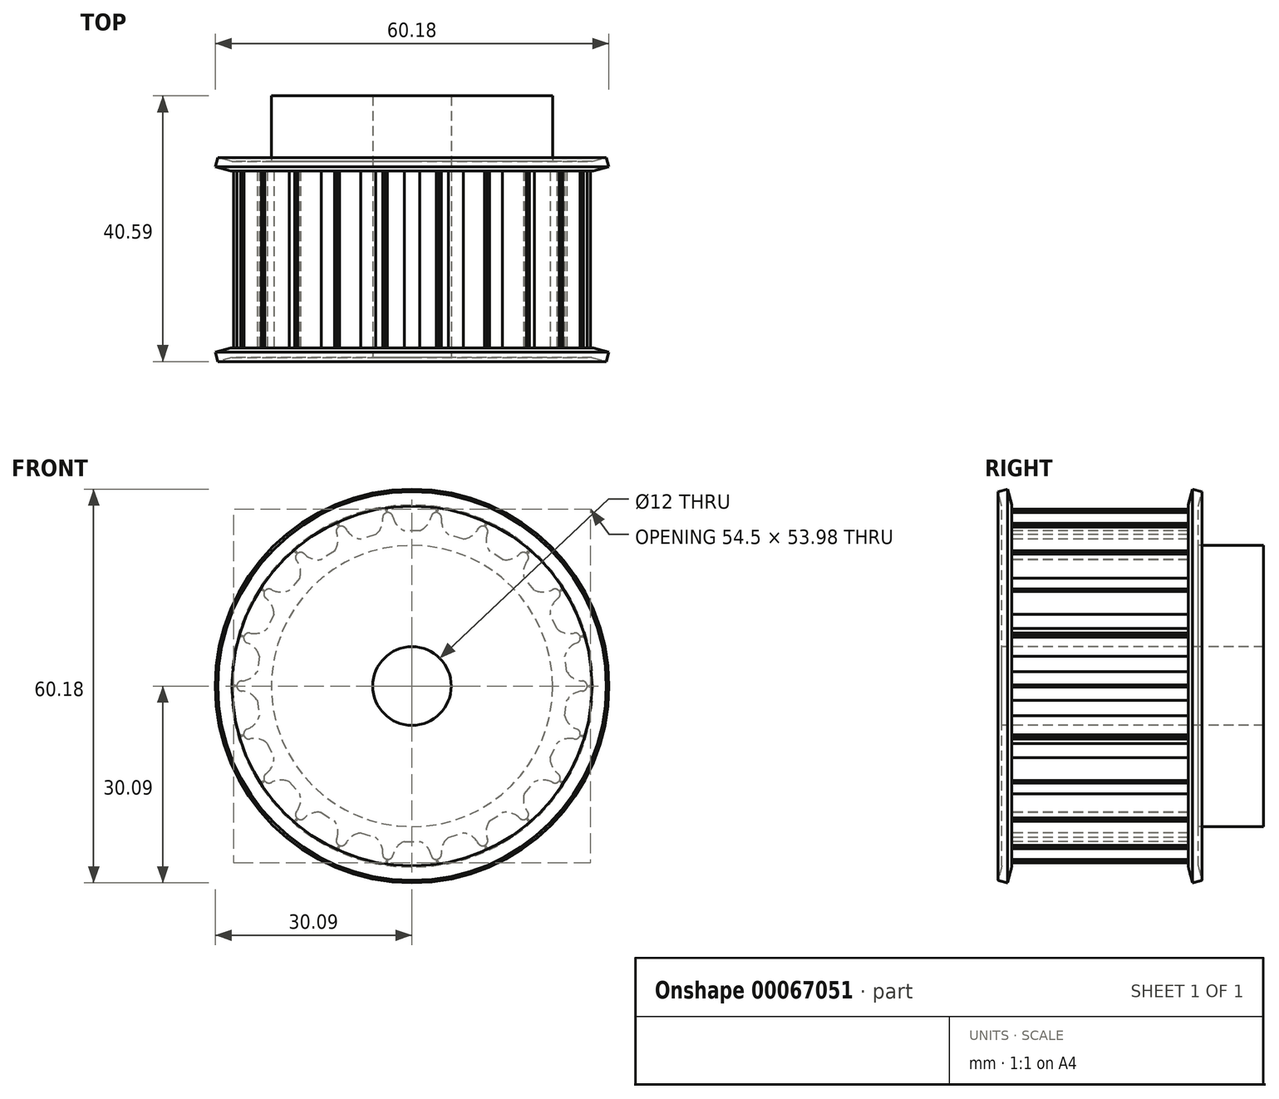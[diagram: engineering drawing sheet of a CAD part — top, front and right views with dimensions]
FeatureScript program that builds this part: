
annotation { "Feature Type Name" : "Feature", "Feature Type Description" : "" }
export const myFeature = defineFeature(function(context is Context, id is Id, definition is map)
    precondition{}
    {
        {
            var Q0;
            Q0=qCreatedBy(makeId("Right.planeOp"),FACE);
            var sketch = newSketch(context, id + "F0", { "sketchPlane" : qUnion([Q0])});
            skLineSegment(sketch, "E0", {"start": v(-21.52, 0) * mm, "end": v(23.89, 0) * mm, "construction": true});
            skLineSegment(sketch, "E1", {"start": v(0, 6) * mm, "end": v(0, 27.25) * mm});
            skLineSegment(sketch, "E2", {"start": v(0, 27.25) * mm, "end": v(30, 27.25) * mm});
            skLineSegment(sketch, "E3", {"start": v(30, 27.25) * mm, "end": v(30, 21.5) * mm});
            skLineSegment(sketch, "E4", {"start": v(30, 21.5) * mm, "end": v(40, 21.5) * mm});
            skLineSegment(sketch, "E5", {"start": v(40, 21.5) * mm, "end": v(40, 6) * mm});
            skLineSegment(sketch, "E6", {"start": v(40, 6) * mm, "end": v(0, 6) * mm});
            skSolve(sketch);
        }
        {
            var Q0;
            Q0=qSketchRegion(id+"F0",true);
            var Q1;
            Q1=sQuery(id+"F0.wireOp",EDGE,"E0");
            revolve(context, id + "F1", {"entities" : qUnion([Q0]), "axis" : qUnion([Q1]), "revolveType" : RevolveType.FULL});
        }
        {
            var Q0;
            Q0=makeQuery(id+"F1.opRevolve","SWEPT_FACE",FACE,{"disambiguationData":[OSD([sQuery(id+"F0.wireOp",EDGE,"E1")])]});
            var sketch = newSketch(context, id + "F2", { "sketchPlane" : qUnion([Q0])});
            skArc(sketch, "E7", {"start": v(-2.94, 25.9) * mm, "mid": v(-2.33, 24.61) * mm, "end": v(-1.2, 23.75) * mm});
            skLineSegment(sketch, "E8.bottom", {"start": v(-3.75, 28.5) * mm, "end": v(3.75, 28.5) * mm});
            skLineSegment(sketch, "E8.top", {"start": v(-3.75, 26.5) * mm, "end": v(-3.67, 26.5) * mm});
            skLineSegment(sketch, "E8.left", {"start": v(-3.75, 28.5) * mm, "end": v(-3.75, 26.5) * mm});
            skLineSegment(sketch, "E8.right", {"start": v(3.75, 28.5) * mm, "end": v(3.75, 26.5) * mm});
            skArc(sketch, "E9.filletArc", {"start": v(-2.94, 25.9) * mm, "mid": v(-3.2, 26.33) * mm, "end": v(-3.67, 26.5) * mm});
            skLineSegment(sketch, "E10", {"start": v(3.67, 26.5) * mm, "end": v(3.75, 26.5) * mm});
            skPoint(sketch, "E11.visualSharp", {"position": v(3, 26.5) * mm});
            skArc(sketch, "E11.filletArc", {"start": v(3.67, 26.5) * mm, "mid": v(3.2, 26.33) * mm, "end": v(2.94, 25.9) * mm});
            skLineSegment(sketch, "E12", {"start": v(-1.2, 23.75) * mm, "end": v(1.2, 23.75) * mm});
            skArc(sketch, "E13.trimOffspring", {"start": v(1.2, 23.75) * mm, "mid": v(2.33, 24.61) * mm, "end": v(2.94, 25.9) * mm});
            skLineSegment(sketch, "E14.1.0", {"start": v(-11.63, 26.29) * mm, "end": v(-4.43, 28.4) * mm});
            skLineSegment(sketch, "E14.1.1", {"start": v(-11.63, 26.29) * mm, "end": v(-11.06, 24.37) * mm});
            skArc(sketch, "E14.1.2", {"start": v(-10.12, 24.02) * mm, "mid": v(-10.49, 24.36) * mm, "end": v(-11, 24.4) * mm});
            skArc(sketch, "E14.1.3", {"start": v(-10.12, 24.02) * mm, "mid": v(-9.17, 22.96) * mm, "end": v(-7.84, 22.45) * mm});
            skLineSegment(sketch, "E14.1.4", {"start": v(-7.84, 22.45) * mm, "end": v(-5.54, 23.13) * mm});
            skArc(sketch, "E14.1.5", {"start": v(-5.54, 23.13) * mm, "mid": v(-4.7, 24.27) * mm, "end": v(-4.48, 25.68) * mm});
            skPoint(sketch, "E14.1.6", {"position": v(-4.59, 26.27) * mm});
            skLineSegment(sketch, "E14.1.7", {"start": v(-4.43, 28.4) * mm, "end": v(-3.87, 26.48) * mm});
            skArc(sketch, "E14.1.8", {"start": v(-3.94, 26.46) * mm, "mid": v(-4.35, 26.17) * mm, "end": v(-4.48, 25.68) * mm});
            skLineSegment(sketch, "E14.2.0", {"start": v(-18.56, 21.95) * mm, "end": v(-12.25, 26) * mm});
            skLineSegment(sketch, "E14.2.1", {"start": v(-18.56, 21.95) * mm, "end": v(-17.48, 20.27) * mm});
            skArc(sketch, "E14.2.2", {"start": v(-16.48, 20.2) * mm, "mid": v(-16.93, 20.42) * mm, "end": v(-17.42, 20.3) * mm});
            skArc(sketch, "E14.2.3", {"start": v(-16.48, 20.2) * mm, "mid": v(-15.27, 19.44) * mm, "end": v(-13.85, 19.33) * mm});
            skLineSegment(sketch, "E14.2.4", {"start": v(-13.85, 19.33) * mm, "end": v(-11.83, 20.63) * mm});
            skArc(sketch, "E14.2.5", {"start": v(-11.83, 20.63) * mm, "mid": v(-11.34, 21.97) * mm, "end": v(-11.53, 23.38) * mm});
            skPoint(sketch, "E14.2.6", {"position": v(-11.8, 23.92) * mm});
            skLineSegment(sketch, "E14.2.7", {"start": v(-12.25, 26) * mm, "end": v(-11.17, 24.32) * mm});
            skArc(sketch, "E14.2.8", {"start": v(-11.24, 24.28) * mm, "mid": v(-11.54, 23.88) * mm, "end": v(-11.53, 23.38) * mm});
            skLineSegment(sketch, "E14.3.0", {"start": v(-24, 15.83) * mm, "end": v(-19.08, 21.5) * mm});
            skLineSegment(sketch, "E14.3.1", {"start": v(-24, 15.83) * mm, "end": v(-22.48, 14.52) * mm});
            skArc(sketch, "E14.3.2", {"start": v(-21.5, 14.74) * mm, "mid": v(-22, 14.82) * mm, "end": v(-22.43, 14.58) * mm});
            skArc(sketch, "E14.3.3", {"start": v(-21.5, 14.74) * mm, "mid": v(-20.13, 14.36) * mm, "end": v(-18.73, 14.65) * mm});
            skLineSegment(sketch, "E14.3.4", {"start": v(-18.73, 14.65) * mm, "end": v(-17.16, 16.46) * mm});
            skArc(sketch, "E14.3.5", {"start": v(-17.16, 16.46) * mm, "mid": v(-17.07, 17.88) * mm, "end": v(-17.65, 19.18) * mm});
            skPoint(sketch, "E14.3.6", {"position": v(-18.06, 19.62) * mm});
            skLineSegment(sketch, "E14.3.7", {"start": v(-19.08, 21.5) * mm, "end": v(-17.57, 20.19) * mm});
            skArc(sketch, "E14.3.8", {"start": v(-17.62, 20.13) * mm, "mid": v(-17.8, 19.66) * mm, "end": v(-17.65, 19.18) * mm});
            skLineSegment(sketch, "E14.4.0", {"start": v(-27.48, 8.43) * mm, "end": v(-24.37, 15.25) * mm});
            skLineSegment(sketch, "E14.4.1", {"start": v(-27.48, 8.43) * mm, "end": v(-25.66, 7.6) * mm});
            skArc(sketch, "E14.4.2", {"start": v(-24.78, 8.09) * mm, "mid": v(-25.28, 8.03) * mm, "end": v(-25.63, 7.67) * mm});
            skArc(sketch, "E14.4.3", {"start": v(-24.78, 8.09) * mm, "mid": v(-23.36, 8.1) * mm, "end": v(-22.1, 8.78) * mm});
            skLineSegment(sketch, "E14.4.4", {"start": v(-22.1, 8.78) * mm, "end": v(-21.1, 10.96) * mm});
            skArc(sketch, "E14.4.5", {"start": v(-21.1, 10.96) * mm, "mid": v(-21.42, 12.35) * mm, "end": v(-22.34, 13.43) * mm});
            skPoint(sketch, "E14.4.6", {"position": v(-22.86, 13.74) * mm});
            skLineSegment(sketch, "E14.4.7", {"start": v(-24.37, 15.25) * mm, "end": v(-22.55, 14.42) * mm});
            skArc(sketch, "E14.4.8", {"start": v(-22.58, 14.35) * mm, "mid": v(-22.62, 13.85) * mm, "end": v(-22.34, 13.43) * mm});
            skLineSegment(sketch, "E14.5.0", {"start": v(-28.74, 0.34) * mm, "end": v(-27.68, 7.77) * mm});
            skLineSegment(sketch, "E14.5.1", {"start": v(-28.74, 0.34) * mm, "end": v(-26.76, 0.06) * mm});
            skArc(sketch, "E14.5.2", {"start": v(-26.05, 0.78) * mm, "mid": v(-26.52, 0.58) * mm, "end": v(-26.75, 0.13) * mm});
            skArc(sketch, "E14.5.3", {"start": v(-26.05, 0.78) * mm, "mid": v(-24.7, 1.2) * mm, "end": v(-23.68, 2.2) * mm});
            skLineSegment(sketch, "E14.5.4", {"start": v(-23.68, 2.2) * mm, "end": v(-23.34, 4.57) * mm});
            skArc(sketch, "E14.5.5", {"start": v(-23.34, 4.57) * mm, "mid": v(-24.03, 5.81) * mm, "end": v(-25.22, 6.6) * mm});
            skPoint(sketch, "E14.5.6", {"position": v(-25.8, 6.74) * mm});
            skLineSegment(sketch, "E14.5.7", {"start": v(-27.68, 7.77) * mm, "end": v(-25.7, 7.48) * mm});
            skArc(sketch, "E14.5.8", {"start": v(-25.7, 7.4) * mm, "mid": v(-25.6, 6.91) * mm, "end": v(-25.22, 6.6) * mm});
            skLineSegment(sketch, "E14.6.0", {"start": v(-27.68, -7.77) * mm, "end": v(-28.74, -0.34) * mm});
            skLineSegment(sketch, "E14.6.1", {"start": v(-27.68, -7.77) * mm, "end": v(-25.7, -7.48) * mm});
            skArc(sketch, "E14.6.2", {"start": v(-25.22, -6.6) * mm, "mid": v(-25.6, -6.91) * mm, "end": v(-25.7, -7.4) * mm});
            skArc(sketch, "E14.6.3", {"start": v(-25.22, -6.6) * mm, "mid": v(-24.03, -5.81) * mm, "end": v(-23.34, -4.57) * mm});
            skLineSegment(sketch, "E14.6.4", {"start": v(-23.34, -4.57) * mm, "end": v(-23.68, -2.2) * mm});
            skArc(sketch, "E14.6.5", {"start": v(-23.68, -2.2) * mm, "mid": v(-24.7, -1.2) * mm, "end": v(-26.05, -0.78) * mm});
            skPoint(sketch, "E14.6.6", {"position": v(-26.66, -0.8) * mm});
            skLineSegment(sketch, "E14.6.7", {"start": v(-28.74, -0.34) * mm, "end": v(-26.76, -0.06) * mm});
            skArc(sketch, "E14.6.8", {"start": v(-26.75, -0.13) * mm, "mid": v(-26.52, -0.58) * mm, "end": v(-26.05, -0.78) * mm});
            skLineSegment(sketch, "E14.7.0", {"start": v(-24.37, -15.25) * mm, "end": v(-27.48, -8.43) * mm});
            skLineSegment(sketch, "E14.7.1", {"start": v(-24.37, -15.25) * mm, "end": v(-22.55, -14.42) * mm});
            skArc(sketch, "E14.7.2", {"start": v(-22.34, -13.43) * mm, "mid": v(-22.62, -13.85) * mm, "end": v(-22.58, -14.35) * mm});
            skArc(sketch, "E14.7.3", {"start": v(-22.34, -13.43) * mm, "mid": v(-21.42, -12.35) * mm, "end": v(-21.1, -10.96) * mm});
            skLineSegment(sketch, "E14.7.4", {"start": v(-21.1, -10.96) * mm, "end": v(-22.1, -8.78) * mm});
            skArc(sketch, "E14.7.5", {"start": v(-22.1, -8.78) * mm, "mid": v(-23.36, -8.1) * mm, "end": v(-24.78, -8.09) * mm});
            skPoint(sketch, "E14.7.6", {"position": v(-25.35, -8.28) * mm});
            skLineSegment(sketch, "E14.7.7", {"start": v(-27.48, -8.43) * mm, "end": v(-25.66, -7.6) * mm});
            skArc(sketch, "E14.7.8", {"start": v(-25.63, -7.67) * mm, "mid": v(-25.28, -8.03) * mm, "end": v(-24.78, -8.09) * mm});
            skLineSegment(sketch, "E14.8.0", {"start": v(-19.08, -21.5) * mm, "end": v(-24, -15.83) * mm});
            skLineSegment(sketch, "E14.8.1", {"start": v(-19.08, -21.5) * mm, "end": v(-17.57, -20.19) * mm});
            skArc(sketch, "E14.8.2", {"start": v(-17.65, -19.18) * mm, "mid": v(-17.8, -19.66) * mm, "end": v(-17.62, -20.13) * mm});
            skArc(sketch, "E14.8.3", {"start": v(-17.65, -19.18) * mm, "mid": v(-17.07, -17.88) * mm, "end": v(-17.16, -16.46) * mm});
            skLineSegment(sketch, "E14.8.4", {"start": v(-17.16, -16.46) * mm, "end": v(-18.73, -14.65) * mm});
            skArc(sketch, "E14.8.5", {"start": v(-18.73, -14.65) * mm, "mid": v(-20.13, -14.36) * mm, "end": v(-21.5, -14.74) * mm});
            skPoint(sketch, "E14.8.6", {"position": v(-22, -15.09) * mm});
            skLineSegment(sketch, "E14.8.7", {"start": v(-24, -15.83) * mm, "end": v(-22.48, -14.52) * mm});
            skArc(sketch, "E14.8.8", {"start": v(-22.43, -14.58) * mm, "mid": v(-22, -14.82) * mm, "end": v(-21.5, -14.74) * mm});
            skLineSegment(sketch, "E14.9.0", {"start": v(-12.25, -26) * mm, "end": v(-18.56, -21.95) * mm});
            skLineSegment(sketch, "E14.9.1", {"start": v(-12.25, -26) * mm, "end": v(-11.17, -24.32) * mm});
            skArc(sketch, "E14.9.2", {"start": v(-11.53, -23.38) * mm, "mid": v(-11.54, -23.88) * mm, "end": v(-11.24, -24.28) * mm});
            skArc(sketch, "E14.9.3", {"start": v(-11.53, -23.38) * mm, "mid": v(-11.34, -21.97) * mm, "end": v(-11.83, -20.63) * mm});
            skLineSegment(sketch, "E14.9.4", {"start": v(-11.83, -20.63) * mm, "end": v(-13.85, -19.33) * mm});
            skArc(sketch, "E14.9.5", {"start": v(-13.85, -19.33) * mm, "mid": v(-15.27, -19.44) * mm, "end": v(-16.48, -20.2) * mm});
            skPoint(sketch, "E14.9.6", {"position": v(-16.85, -20.67) * mm});
            skLineSegment(sketch, "E14.9.7", {"start": v(-18.56, -21.95) * mm, "end": v(-17.48, -20.27) * mm});
            skArc(sketch, "E14.9.8", {"start": v(-17.42, -20.3) * mm, "mid": v(-16.93, -20.42) * mm, "end": v(-16.48, -20.2) * mm});
            skLineSegment(sketch, "E14.10.0", {"start": v(-4.43, -28.4) * mm, "end": v(-11.63, -26.29) * mm});
            skLineSegment(sketch, "E14.10.1", {"start": v(-4.43, -28.4) * mm, "end": v(-3.87, -26.48) * mm});
            skArc(sketch, "E14.10.2", {"start": v(-4.48, -25.68) * mm, "mid": v(-4.35, -26.17) * mm, "end": v(-3.94, -26.46) * mm});
            skArc(sketch, "E14.10.3", {"start": v(-4.48, -25.68) * mm, "mid": v(-4.7, -24.27) * mm, "end": v(-5.54, -23.13) * mm});
            skLineSegment(sketch, "E14.10.4", {"start": v(-5.54, -23.13) * mm, "end": v(-7.84, -22.45) * mm});
            skArc(sketch, "E14.10.5", {"start": v(-7.84, -22.45) * mm, "mid": v(-9.17, -22.96) * mm, "end": v(-10.12, -24.02) * mm});
            skPoint(sketch, "E14.10.6", {"position": v(-10.34, -24.58) * mm});
            skLineSegment(sketch, "E14.10.7", {"start": v(-11.63, -26.29) * mm, "end": v(-11.06, -24.37) * mm});
            skArc(sketch, "E14.10.8", {"start": v(-11, -24.4) * mm, "mid": v(-10.49, -24.36) * mm, "end": v(-10.12, -24.02) * mm});
            skLineSegment(sketch, "E14.11.0", {"start": v(3.75, -28.5) * mm, "end": v(-3.75, -28.5) * mm});
            skLineSegment(sketch, "E14.11.1", {"start": v(3.75, -28.5) * mm, "end": v(3.75, -26.5) * mm});
            skArc(sketch, "E14.11.2", {"start": v(2.94, -25.9) * mm, "mid": v(3.2, -26.33) * mm, "end": v(3.67, -26.5) * mm});
            skArc(sketch, "E14.11.3", {"start": v(2.94, -25.9) * mm, "mid": v(2.33, -24.61) * mm, "end": v(1.2, -23.75) * mm});
            skLineSegment(sketch, "E14.11.4", {"start": v(1.2, -23.75) * mm, "end": v(-1.2, -23.75) * mm});
            skArc(sketch, "E14.11.5", {"start": v(-1.2, -23.75) * mm, "mid": v(-2.33, -24.61) * mm, "end": v(-2.94, -25.9) * mm});
            skPoint(sketch, "E14.11.6", {"position": v(-3, -26.5) * mm});
            skLineSegment(sketch, "E14.11.7", {"start": v(-3.75, -28.5) * mm, "end": v(-3.75, -26.5) * mm});
            skArc(sketch, "E14.11.8", {"start": v(-3.67, -26.5) * mm, "mid": v(-3.2, -26.33) * mm, "end": v(-2.94, -25.9) * mm});
            skLineSegment(sketch, "E14.12.0", {"start": v(11.63, -26.29) * mm, "end": v(4.43, -28.4) * mm});
            skLineSegment(sketch, "E14.12.1", {"start": v(11.63, -26.29) * mm, "end": v(11.06, -24.37) * mm});
            skArc(sketch, "E14.12.2", {"start": v(10.12, -24.02) * mm, "mid": v(10.49, -24.36) * mm, "end": v(11, -24.4) * mm});
            skArc(sketch, "E14.12.3", {"start": v(10.12, -24.02) * mm, "mid": v(9.17, -22.96) * mm, "end": v(7.84, -22.45) * mm});
            skLineSegment(sketch, "E14.12.4", {"start": v(7.84, -22.45) * mm, "end": v(5.54, -23.13) * mm});
            skArc(sketch, "E14.12.5", {"start": v(5.54, -23.13) * mm, "mid": v(4.7, -24.27) * mm, "end": v(4.48, -25.68) * mm});
            skPoint(sketch, "E14.12.6", {"position": v(4.59, -26.27) * mm});
            skLineSegment(sketch, "E14.12.7", {"start": v(4.43, -28.4) * mm, "end": v(3.87, -26.48) * mm});
            skArc(sketch, "E14.12.8", {"start": v(3.94, -26.46) * mm, "mid": v(4.35, -26.17) * mm, "end": v(4.48, -25.68) * mm});
            skLineSegment(sketch, "E14.13.0", {"start": v(18.56, -21.95) * mm, "end": v(12.25, -26) * mm});
            skLineSegment(sketch, "E14.13.1", {"start": v(18.56, -21.95) * mm, "end": v(17.48, -20.27) * mm});
            skArc(sketch, "E14.13.2", {"start": v(16.48, -20.2) * mm, "mid": v(16.93, -20.42) * mm, "end": v(17.42, -20.3) * mm});
            skArc(sketch, "E14.13.3", {"start": v(16.48, -20.2) * mm, "mid": v(15.27, -19.44) * mm, "end": v(13.85, -19.33) * mm});
            skLineSegment(sketch, "E14.13.4", {"start": v(13.85, -19.33) * mm, "end": v(11.83, -20.63) * mm});
            skArc(sketch, "E14.13.5", {"start": v(11.83, -20.63) * mm, "mid": v(11.34, -21.97) * mm, "end": v(11.53, -23.38) * mm});
            skPoint(sketch, "E14.13.6", {"position": v(11.8, -23.92) * mm});
            skLineSegment(sketch, "E14.13.7", {"start": v(12.25, -26) * mm, "end": v(11.17, -24.32) * mm});
            skArc(sketch, "E14.13.8", {"start": v(11.24, -24.28) * mm, "mid": v(11.54, -23.88) * mm, "end": v(11.53, -23.38) * mm});
            skLineSegment(sketch, "E14.14.0", {"start": v(24, -15.83) * mm, "end": v(19.08, -21.5) * mm});
            skLineSegment(sketch, "E14.14.1", {"start": v(24, -15.83) * mm, "end": v(22.48, -14.52) * mm});
            skArc(sketch, "E14.14.2", {"start": v(21.5, -14.74) * mm, "mid": v(22, -14.82) * mm, "end": v(22.43, -14.58) * mm});
            skArc(sketch, "E14.14.3", {"start": v(21.5, -14.74) * mm, "mid": v(20.13, -14.36) * mm, "end": v(18.73, -14.65) * mm});
            skLineSegment(sketch, "E14.14.4", {"start": v(18.73, -14.65) * mm, "end": v(17.16, -16.46) * mm});
            skArc(sketch, "E14.14.5", {"start": v(17.16, -16.46) * mm, "mid": v(17.07, -17.88) * mm, "end": v(17.65, -19.18) * mm});
            skPoint(sketch, "E14.14.6", {"position": v(18.06, -19.62) * mm});
            skLineSegment(sketch, "E14.14.7", {"start": v(19.08, -21.5) * mm, "end": v(17.57, -20.19) * mm});
            skArc(sketch, "E14.14.8", {"start": v(17.62, -20.13) * mm, "mid": v(17.8, -19.66) * mm, "end": v(17.65, -19.18) * mm});
            skLineSegment(sketch, "E14.15.0", {"start": v(27.48, -8.43) * mm, "end": v(24.37, -15.25) * mm});
            skLineSegment(sketch, "E14.15.1", {"start": v(27.48, -8.43) * mm, "end": v(25.66, -7.6) * mm});
            skArc(sketch, "E14.15.2", {"start": v(24.78, -8.09) * mm, "mid": v(25.28, -8.03) * mm, "end": v(25.63, -7.67) * mm});
            skArc(sketch, "E14.15.3", {"start": v(24.78, -8.09) * mm, "mid": v(23.36, -8.1) * mm, "end": v(22.1, -8.78) * mm});
            skLineSegment(sketch, "E14.15.4", {"start": v(22.1, -8.78) * mm, "end": v(21.1, -10.96) * mm});
            skArc(sketch, "E14.15.5", {"start": v(21.1, -10.96) * mm, "mid": v(21.42, -12.35) * mm, "end": v(22.34, -13.43) * mm});
            skPoint(sketch, "E14.15.6", {"position": v(22.86, -13.74) * mm});
            skLineSegment(sketch, "E14.15.7", {"start": v(24.37, -15.25) * mm, "end": v(22.55, -14.42) * mm});
            skArc(sketch, "E14.15.8", {"start": v(22.58, -14.35) * mm, "mid": v(22.62, -13.85) * mm, "end": v(22.34, -13.43) * mm});
            skLineSegment(sketch, "E14.16.0", {"start": v(28.74, -0.34) * mm, "end": v(27.68, -7.77) * mm});
            skLineSegment(sketch, "E14.16.1", {"start": v(28.74, -0.34) * mm, "end": v(26.76, -0.06) * mm});
            skArc(sketch, "E14.16.2", {"start": v(26.05, -0.78) * mm, "mid": v(26.52, -0.58) * mm, "end": v(26.75, -0.13) * mm});
            skArc(sketch, "E14.16.3", {"start": v(26.05, -0.78) * mm, "mid": v(24.7, -1.2) * mm, "end": v(23.68, -2.2) * mm});
            skLineSegment(sketch, "E14.16.4", {"start": v(23.68, -2.2) * mm, "end": v(23.34, -4.57) * mm});
            skArc(sketch, "E14.16.5", {"start": v(23.34, -4.57) * mm, "mid": v(24.03, -5.81) * mm, "end": v(25.22, -6.6) * mm});
            skPoint(sketch, "E14.16.6", {"position": v(25.8, -6.74) * mm});
            skLineSegment(sketch, "E14.16.7", {"start": v(27.68, -7.77) * mm, "end": v(25.7, -7.48) * mm});
            skArc(sketch, "E14.16.8", {"start": v(25.7, -7.4) * mm, "mid": v(25.6, -6.91) * mm, "end": v(25.22, -6.6) * mm});
            skLineSegment(sketch, "E14.17.0", {"start": v(27.68, 7.77) * mm, "end": v(28.74, 0.34) * mm});
            skLineSegment(sketch, "E14.17.1", {"start": v(27.68, 7.77) * mm, "end": v(25.7, 7.48) * mm});
            skArc(sketch, "E14.17.2", {"start": v(25.22, 6.6) * mm, "mid": v(25.6, 6.91) * mm, "end": v(25.7, 7.4) * mm});
            skArc(sketch, "E14.17.3", {"start": v(25.22, 6.6) * mm, "mid": v(24.03, 5.81) * mm, "end": v(23.34, 4.57) * mm});
            skLineSegment(sketch, "E14.17.4", {"start": v(23.34, 4.57) * mm, "end": v(23.68, 2.2) * mm});
            skArc(sketch, "E14.17.5", {"start": v(23.68, 2.2) * mm, "mid": v(24.7, 1.2) * mm, "end": v(26.05, 0.78) * mm});
            skPoint(sketch, "E14.17.6", {"position": v(26.66, 0.8) * mm});
            skLineSegment(sketch, "E14.17.7", {"start": v(28.74, 0.34) * mm, "end": v(26.76, 0.06) * mm});
            skArc(sketch, "E14.17.8", {"start": v(26.75, 0.13) * mm, "mid": v(26.52, 0.58) * mm, "end": v(26.05, 0.78) * mm});
            skLineSegment(sketch, "E14.18.0", {"start": v(24.37, 15.25) * mm, "end": v(27.48, 8.43) * mm});
            skLineSegment(sketch, "E14.18.1", {"start": v(24.37, 15.25) * mm, "end": v(22.55, 14.42) * mm});
            skArc(sketch, "E14.18.2", {"start": v(22.34, 13.43) * mm, "mid": v(22.62, 13.85) * mm, "end": v(22.58, 14.35) * mm});
            skArc(sketch, "E14.18.3", {"start": v(22.34, 13.43) * mm, "mid": v(21.42, 12.35) * mm, "end": v(21.1, 10.96) * mm});
            skLineSegment(sketch, "E14.18.4", {"start": v(21.1, 10.96) * mm, "end": v(22.1, 8.78) * mm});
            skArc(sketch, "E14.18.5", {"start": v(22.1, 8.78) * mm, "mid": v(23.36, 8.1) * mm, "end": v(24.78, 8.09) * mm});
            skPoint(sketch, "E14.18.6", {"position": v(25.35, 8.28) * mm});
            skLineSegment(sketch, "E14.18.7", {"start": v(27.48, 8.43) * mm, "end": v(25.66, 7.6) * mm});
            skArc(sketch, "E14.18.8", {"start": v(25.63, 7.67) * mm, "mid": v(25.28, 8.03) * mm, "end": v(24.78, 8.09) * mm});
            skLineSegment(sketch, "E14.19.0", {"start": v(19.08, 21.5) * mm, "end": v(24, 15.83) * mm});
            skLineSegment(sketch, "E14.19.1", {"start": v(19.08, 21.5) * mm, "end": v(17.57, 20.19) * mm});
            skArc(sketch, "E14.19.2", {"start": v(17.65, 19.18) * mm, "mid": v(17.8, 19.66) * mm, "end": v(17.62, 20.13) * mm});
            skArc(sketch, "E14.19.3", {"start": v(17.65, 19.18) * mm, "mid": v(17.07, 17.88) * mm, "end": v(17.16, 16.46) * mm});
            skLineSegment(sketch, "E14.19.4", {"start": v(17.16, 16.46) * mm, "end": v(18.73, 14.65) * mm});
            skArc(sketch, "E14.19.5", {"start": v(18.73, 14.65) * mm, "mid": v(20.13, 14.36) * mm, "end": v(21.5, 14.74) * mm});
            skPoint(sketch, "E14.19.6", {"position": v(22, 15.09) * mm});
            skLineSegment(sketch, "E14.19.7", {"start": v(24, 15.83) * mm, "end": v(22.48, 14.52) * mm});
            skArc(sketch, "E14.19.8", {"start": v(22.43, 14.58) * mm, "mid": v(22, 14.82) * mm, "end": v(21.5, 14.74) * mm});
            skLineSegment(sketch, "E14.20.0", {"start": v(12.25, 26) * mm, "end": v(18.56, 21.95) * mm});
            skLineSegment(sketch, "E14.20.1", {"start": v(12.25, 26) * mm, "end": v(11.17, 24.32) * mm});
            skArc(sketch, "E14.20.2", {"start": v(11.53, 23.38) * mm, "mid": v(11.54, 23.88) * mm, "end": v(11.24, 24.28) * mm});
            skArc(sketch, "E14.20.3", {"start": v(11.53, 23.38) * mm, "mid": v(11.34, 21.97) * mm, "end": v(11.83, 20.63) * mm});
            skLineSegment(sketch, "E14.20.4", {"start": v(11.83, 20.63) * mm, "end": v(13.85, 19.33) * mm});
            skArc(sketch, "E14.20.5", {"start": v(13.85, 19.33) * mm, "mid": v(15.27, 19.44) * mm, "end": v(16.48, 20.2) * mm});
            skPoint(sketch, "E14.20.6", {"position": v(16.85, 20.67) * mm});
            skLineSegment(sketch, "E14.20.7", {"start": v(18.56, 21.95) * mm, "end": v(17.48, 20.27) * mm});
            skArc(sketch, "E14.20.8", {"start": v(17.42, 20.3) * mm, "mid": v(16.93, 20.42) * mm, "end": v(16.48, 20.2) * mm});
            skLineSegment(sketch, "E14.21.0", {"start": v(4.43, 28.4) * mm, "end": v(11.63, 26.29) * mm});
            skLineSegment(sketch, "E14.21.1", {"start": v(4.43, 28.4) * mm, "end": v(3.87, 26.48) * mm});
            skArc(sketch, "E14.21.2", {"start": v(4.48, 25.68) * mm, "mid": v(4.35, 26.17) * mm, "end": v(3.94, 26.46) * mm});
            skArc(sketch, "E14.21.3", {"start": v(4.48, 25.68) * mm, "mid": v(4.7, 24.27) * mm, "end": v(5.54, 23.13) * mm});
            skLineSegment(sketch, "E14.21.4", {"start": v(5.54, 23.13) * mm, "end": v(7.84, 22.45) * mm});
            skArc(sketch, "E14.21.5", {"start": v(7.84, 22.45) * mm, "mid": v(9.17, 22.96) * mm, "end": v(10.12, 24.02) * mm});
            skPoint(sketch, "E14.21.6", {"position": v(10.34, 24.58) * mm});
            skLineSegment(sketch, "E14.21.7", {"start": v(11.63, 26.29) * mm, "end": v(11.06, 24.37) * mm});
            skArc(sketch, "E14.21.8", {"start": v(11, 24.4) * mm, "mid": v(10.49, 24.36) * mm, "end": v(10.12, 24.02) * mm});
            skPoint(sketch, "E14.center", {"position": v(0, 0) * mm});
            skLineSegment(sketch, "E15", {"start": v(-11.06, 24.37) * mm, "end": v(-11, 24.4) * mm});
            skLineSegment(sketch, "E16", {"start": v(-11.24, 24.28) * mm, "end": v(-11.17, 24.32) * mm});
            skLineSegment(sketch, "E17", {"start": v(-17.48, 20.27) * mm, "end": v(-17.42, 20.3) * mm});
            skLineSegment(sketch, "E18", {"start": v(-17.62, 20.13) * mm, "end": v(-17.57, 20.19) * mm});
            skLineSegment(sketch, "E19", {"start": v(-3.94, 26.46) * mm, "end": v(-3.87, 26.48) * mm});
            skLineSegment(sketch, "E20", {"start": v(3.87, 26.48) * mm, "end": v(3.94, 26.46) * mm});
            skLineSegment(sketch, "E21", {"start": v(11, 24.4) * mm, "end": v(11.06, 24.37) * mm});
            skLineSegment(sketch, "E22", {"start": v(11.17, 24.32) * mm, "end": v(11.24, 24.28) * mm});
            skLineSegment(sketch, "E23", {"start": v(17.42, 20.3) * mm, "end": v(17.48, 20.27) * mm});
            skLineSegment(sketch, "E24", {"start": v(17.57, 20.19) * mm, "end": v(17.62, 20.13) * mm});
            skLineSegment(sketch, "E25", {"start": v(22.43, 14.58) * mm, "end": v(22.48, 14.52) * mm});
            skLineSegment(sketch, "E26", {"start": v(22.55, 14.42) * mm, "end": v(22.58, 14.35) * mm});
            skLineSegment(sketch, "E27", {"start": v(25.63, 7.67) * mm, "end": v(25.66, 7.6) * mm});
            skLineSegment(sketch, "E28", {"start": v(25.7, 7.48) * mm, "end": v(25.7, 7.4) * mm});
            skLineSegment(sketch, "E29", {"start": v(26.75, 0.13) * mm, "end": v(26.76, 0.06) * mm});
            skLineSegment(sketch, "E30", {"start": v(26.76, -0.06) * mm, "end": v(26.75, -0.13) * mm});
            skLineSegment(sketch, "E31", {"start": v(25.7, -7.4) * mm, "end": v(25.7, -7.48) * mm});
            skLineSegment(sketch, "E32", {"start": v(25.66, -7.6) * mm, "end": v(25.63, -7.67) * mm});
            skLineSegment(sketch, "E33", {"start": v(22.58, -14.35) * mm, "end": v(22.55, -14.42) * mm});
            skLineSegment(sketch, "E34", {"start": v(22.48, -14.52) * mm, "end": v(22.43, -14.58) * mm});
            skLineSegment(sketch, "E35", {"start": v(17.42, -20.3) * mm, "end": v(17.48, -20.27) * mm});
            skLineSegment(sketch, "E36", {"start": v(17.57, -20.19) * mm, "end": v(17.62, -20.13) * mm});
            skLineSegment(sketch, "E37", {"start": v(11, -24.4) * mm, "end": v(11.06, -24.37) * mm});
            skLineSegment(sketch, "E38", {"start": v(11.17, -24.32) * mm, "end": v(11.24, -24.28) * mm});
            skLineSegment(sketch, "E39", {"start": v(3.67, -26.5) * mm, "end": v(3.75, -26.5) * mm});
            skLineSegment(sketch, "E40", {"start": v(3.87, -26.48) * mm, "end": v(3.94, -26.46) * mm});
            skLineSegment(sketch, "E41", {"start": v(-3.94, -26.46) * mm, "end": v(-3.87, -26.48) * mm});
            skLineSegment(sketch, "E42", {"start": v(-3.75, -26.5) * mm, "end": v(-3.67, -26.5) * mm});
            skLineSegment(sketch, "E43", {"start": v(-11.24, -24.28) * mm, "end": v(-11.17, -24.32) * mm});
            skLineSegment(sketch, "E44", {"start": v(-11.06, -24.37) * mm, "end": v(-11, -24.4) * mm});
            skLineSegment(sketch, "E45", {"start": v(-17.62, -20.13) * mm, "end": v(-17.57, -20.19) * mm});
            skLineSegment(sketch, "E46", {"start": v(-17.48, -20.27) * mm, "end": v(-17.42, -20.3) * mm});
            skLineSegment(sketch, "E47", {"start": v(-22.58, -14.35) * mm, "end": v(-22.55, -14.42) * mm});
            skLineSegment(sketch, "E48", {"start": v(-22.48, -14.52) * mm, "end": v(-22.43, -14.58) * mm});
            skLineSegment(sketch, "E49", {"start": v(-25.7, -7.4) * mm, "end": v(-25.7, -7.48) * mm});
            skLineSegment(sketch, "E50", {"start": v(-25.66, -7.6) * mm, "end": v(-25.63, -7.67) * mm});
            skLineSegment(sketch, "E51", {"start": v(-26.76, -0.06) * mm, "end": v(-26.75, -0.13) * mm});
            skLineSegment(sketch, "E52", {"start": v(-26.75, 0.13) * mm, "end": v(-26.76, 0.06) * mm});
            skLineSegment(sketch, "E53", {"start": v(-25.63, 7.67) * mm, "end": v(-25.66, 7.6) * mm});
            skLineSegment(sketch, "E54", {"start": v(-25.7, 7.48) * mm, "end": v(-25.7, 7.4) * mm});
            skLineSegment(sketch, "E55", {"start": v(-22.43, 14.58) * mm, "end": v(-22.48, 14.52) * mm});
            skLineSegment(sketch, "E56", {"start": v(-22.55, 14.42) * mm, "end": v(-22.58, 14.35) * mm});
            skSolve(sketch);
        }
        {
            var Q0;
            Q0=qSketchRegion(id+"F2",true);
            extrude(context, id + "F3", {"entities" : qUnion([Q0]), "operationType" : NewBodyOperationType.REMOVE, "endBound" : BoundingType.THROUGH_ALL, "oppositeDirection" : true, "depth" : 25.4 * mm});
        }
        {
            var Q0;
            Q0=qCreatedBy(makeId("Right.planeOp"),FACE);
            var sketch = newSketch(context, id + "F4", { "sketchPlane" : qUnion([Q0])});
            skLineSegment(sketch, "E57.bottom", {"start": v(0, 22.7) * mm, "end": v(1.5, 22.7) * mm});
            skLineSegment(sketch, "E57.top", {"start": v(0, 27.7) * mm, "end": v(1.5, 27.7) * mm});
            skLineSegment(sketch, "E57.left", {"start": v(0, 22.7) * mm, "end": v(0, 27.7) * mm});
            skLineSegment(sketch, "E57.right", {"start": v(1.5, 22.7) * mm, "end": v(1.5, 27.7) * mm});
            skLineSegment(sketch, "E58", {"start": v(15, 41.03) * mm, "end": v(15, -28.92) * mm, "construction": true});
            skLineSegment(sketch, "E59.MirrorCS", {"start": v(28.5, 22.7) * mm, "end": v(28.5, 27.7) * mm});
            skLineSegment(sketch, "E60.MirrorCS", {"start": v(30, 22.7) * mm, "end": v(28.5, 22.7) * mm});
            skLineSegment(sketch, "E61.MirrorCS", {"start": v(30, 22.7) * mm, "end": v(30, 27.7) * mm});
            skLineSegment(sketch, "E62.MirrorCS", {"start": v(30, 27.7) * mm, "end": v(28.5, 27.7) * mm});
            skLineSegment(sketch, "E63", {"start": v(1.5, 27.7) * mm, "end": v(0.86, 30.1) * mm});
            skLineSegment(sketch, "E64", {"start": v(0.86, 30.1) * mm, "end": v(-0.6, 29.7) * mm});
            skLineSegment(sketch, "E65", {"start": v(-0.6, 29.7) * mm, "end": v(0.05, 27.3) * mm});
            skLineSegment(sketch, "E66", {"start": v(0.05, 27.3) * mm, "end": v(1.5, 27.7) * mm});
            skLineSegment(sketch, "E67.MirrorCS", {"start": v(29.14, 30.1) * mm, "end": v(30.6, 29.7) * mm});
            skLineSegment(sketch, "E68.MirrorCS", {"start": v(30.6, 29.7) * mm, "end": v(29.95, 27.3) * mm});
            skLineSegment(sketch, "E69.MirrorCS", {"start": v(28.5, 27.7) * mm, "end": v(29.14, 30.1) * mm});
            skLineSegment(sketch, "E70.MirrorCS", {"start": v(29.95, 27.3) * mm, "end": v(28.5, 27.7) * mm});
            skSolve(sketch);
        }
        {
            var Q0;
            Q0=qCreatedBy(makeId("Right.planeOp"),FACE);
            var sketch = newSketch(context, id + "F5", { "sketchPlane" : qUnion([Q0])});
            skLineSegment(sketch, "E71", {"start": v(-38.96, 0) * mm, "end": v(60.95, 0) * mm, "construction": true});
            skSolve(sketch);
        }
        {
            var Q0;
            Q0=qSketchRegion(id+"F4",true);
            var Q1;
            Q1=sQuery(id+"F5.wireOp",EDGE,"E71");
            revolve(context, id + "F6", {"operationType" : NewBodyOperationType.ADD, "entities" : qUnion([Q0]), "axis" : qUnion([Q1]), "revolveType" : RevolveType.FULL});
        }
    });
